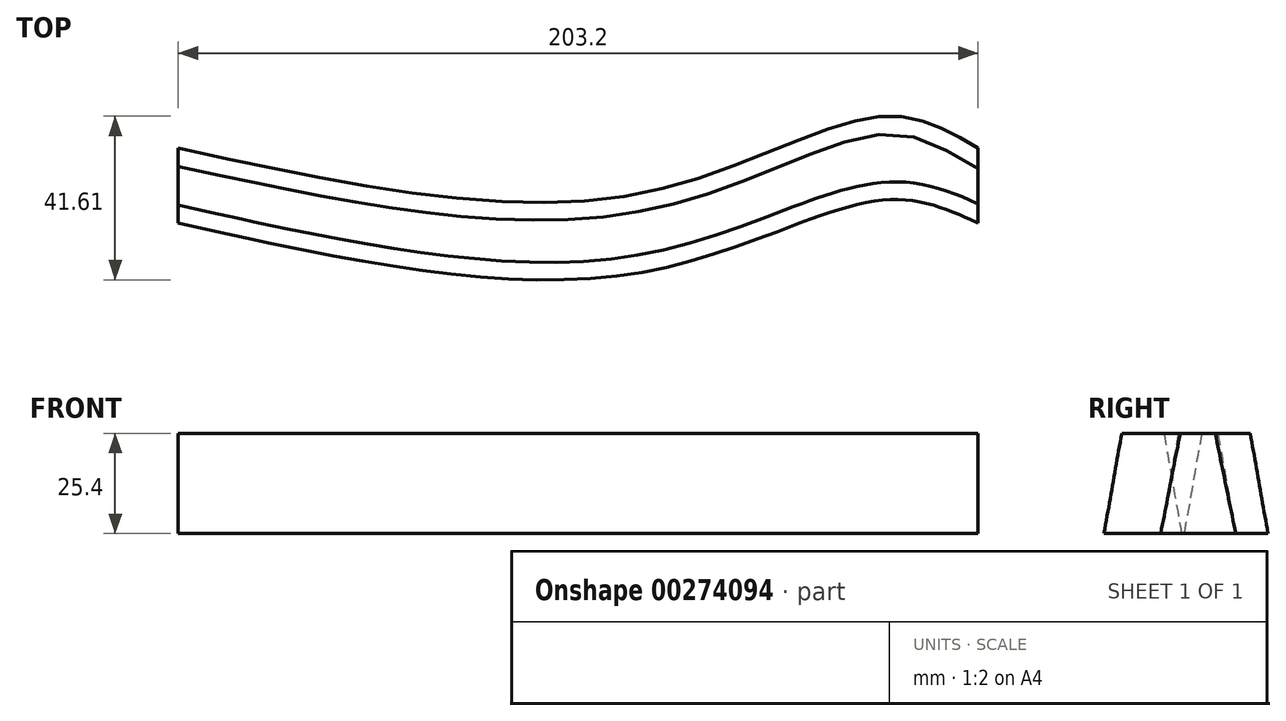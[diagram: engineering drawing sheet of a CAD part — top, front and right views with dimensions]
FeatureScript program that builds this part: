
annotation { "Feature Type Name" : "Feature", "Feature Type Description" : "" }
export const myFeature = defineFeature(function(context is Context, id is Id, definition is map)
    precondition{}
    {
        {
            var Q0;
            Q0=qCreatedBy(makeId("Top.planeOp"),FACE);
            var sketch = newSketch(context, id + "F0", { "sketchPlane" : qUnion([Q0])});
            skLineSegment(sketch, "E0", {"start": v(-50.7, -2.78) * mm, "end": v(-50.7, -21.83) * mm});
            skLineSegment(sketch, "E1", {"start": v(-50.7, -21.83) * mm, "end": v(152.5, -21.83) * mm});
            skLineSegment(sketch, "E2", {"start": v(152.5, -21.83) * mm, "end": v(152.5, -2.78) * mm});
            skFitSpline(sketch, "E3", {"points": [v(-50.7, -21.83) * mm, v(66.82, -34.36) * mm, v(128.15, -15.94) * mm, v(152.5, -21.83) * mm], "startDerivative": vector(274.94, -60.81) * mm, "endDerivative": vector(105.68, -48.77) * mm});
            skFitSpline(sketch, "E4", {"points": [v(-50.7, -2.78) * mm, v(66.82, -14.24) * mm, v(128.15, 5.32) * mm, v(152.5, -2.78) * mm], "startDerivative": vector(276.04, -60.1) * mm, "endDerivative": vector(104.4, -62.01) * mm});
            skSolve(sketch);
        }
        {
            var Q0;
            {var subQ0=sQuery(id+"F0.wireOp",EDGE,"E0");Q0=makeQuery(id+"F0.imprint","IMPRINT",FACE,{"disambiguationData":[TD([[makeQuery(id+"F0.imprint","IMPRINT",EDGE,{"derivedFrom":subQ0}),1.0]])]});}
            var Q1;
            {var subQ0=sQuery(id+"F0.wireOp",EDGE,"6b57bacd-f98f-4d05-8f3f-914d58afb215");var subQ1=sQuery(id+"F0.wireOp",EDGE,"E1");var subQ2=makeQuery(id+"F0.imprint","INTERSECT",VERTEX,{"disambiguationData":[OD(0.0)],"derivedFrom":[subQ1,subQ0]});Q1=makeQuery(id+"F0.imprint","IMPRINT",FACE,{"disambiguationData":[TD([[makeQuery(id+"F0.imprint","IMPRINT",EDGE,{"disambiguationData":[TD([[subQ2,-1.0]])],"derivedFrom":subQ1}),-1.0]])]});}
            var Q2;
            {var subQ5=sQuery(id+"F0.wireOp",EDGE,"E2");Q2=makeQuery(id+"F0.imprint","IMPRINT",FACE,{"disambiguationData":[TD([[makeQuery(id+"F0.imprint","IMPRINT",EDGE,{"derivedFrom":subQ5}),1.0]])]});}
            var Q3;
            {var subQ1=sQuery(id+"F0.wireOp",EDGE,"E1");var subQ3=sQuery(id+"F0.wireOp",EDGE,"6b57bacd-f98f-4d05-8f3f-914d58afb215");var subQ5=makeQuery(id+"F0.imprint","INTERSECT",VERTEX,{"disambiguationData":[OD(1.0)],"derivedFrom":[subQ1,subQ3]});Q3=makeQuery(id+"F0.imprint","IMPRINT",FACE,{"disambiguationData":[TD([[makeQuery(id+"F0.imprint","IMPRINT",EDGE,{"disambiguationData":[TD([[subQ5,-1.0]])],"derivedFrom":subQ1}),-1.0]])]});}
            var Q4;
            {var subQ0=sQuery(id+"F0.wireOp",EDGE,"E3");var subQ1=sQuery(id+"F0.wireOp",EDGE,"E1");var subQ3=makeQuery(id+"F0.imprint","INTERSECT",VERTEX,{"derivedFrom":[subQ1,subQ0]});Q4=makeQuery(id+"F0.imprint","IMPRINT",FACE,{"disambiguationData":[TD([[makeQuery(id+"F0.imprint","IMPRINT",EDGE,{"disambiguationData":[TD([[subQ3,1.0]])],"derivedFrom":subQ1}),-1.0]])]});}
            extrude(context, id + "F1", {"entities" : qUnion([Q0, Q1, Q2, Q3, Q4]), "depth" : 25.4 * mm});
        }
        {
            var Q0;
            Q0=makeQuery(id+"F1.opExtrude","CAP_EDGE",EDGE,{"disambiguationData":[OSD([sQuery(id+"F0.wireOp",EDGE,"E3")])],"isStart":false});
            var Q1;
            Q1=makeQuery(id+"F1.opExtrude","CAP_EDGE",EDGE,{"disambiguationData":[OSD([sQuery(id+"F0.wireOp",EDGE,"E4")])],"isStart":false});
            chamfer(context, id + "F2", {"entities" : qUnion([Q0, Q1]), "chamferType" : ChamferType.OFFSET_ANGLE, "width" : 25.4 * mm, "oppositeDirection" : true, "angle" : 10 * degree, "tangentPropagation" : true});
        }
    });
